# Revit family: LBL-VL
name_source: partatom
category: Lighting Fixtures
units: mm (PartAtom-declared; Revit-internal decimal feet)

## family parameters
Always vertical = Yes
Cut with Voids When Loaded = No
Host = Ceiling
Light Source = Yes
OmniClass Number = 23.80.70.11.14.11
OmniClass Title = Downlights
Part Type = Normal
Room Calculation Point = No
Round Connector Dimension = Use Diameter
Shared = No

## types (8) — shared parameters
Assembly Code = D5020200
Color Filter = 16777215
Description = Commercial-grade, surface or suspended-mounted wrap-around ceiling luminaire
Dimming Lamp Color Temperature Shift = <None>
Housing Finish = Metal - Viscor - White
Lamp = LED
Lens Finish = Polycarbonate - Viscor - Frosted Round
Manufacturer = VISIONEERING by VISCOR
Model = LBL-VL
URL = https://www.viscor.com
Voltage = 120 V
Width = 0' - 8"

## per-type parameters (varying)
| type | Apparent Load | Emit from Line Length | Lamp Wattage | Length | Photometric Web File | Tilt Angle |
| LBL-VL24-LED840K028LUNV | 22 VA | 1' - 11 3/8" | 22 VA | 1' - 11 3/8" | LBL-VL24-LED840K028LUNV.IES | 90.00° |
| LBL-VL24-LED840K037LUNV | 29 VA | 1' - 11 3/8" | 29 VA | 1' - 11 3/8" | LBL-VL24-LED840K037LUNV.IES | 90.00° |
| LBL-VL48-LED840K028LUNV | 22 VA | 3' - 10 1/16" | 22 VA | 3' - 10 1/16" | LBL-VL48-LED840K028LUNV.IES | 90.00° |
| LBL-VL48-LED840K037LUNV | 29 VA | 3' - 10 1/16" | 29 VA | 3' - 10 1/16" | LBL-VL48-LED840K037LUNV.IES | 90.00° |
| LBL-VL48-LED840K045LUNV | 34 VA | 3' - 10 1/16" | 34 VA | 3' - 10 1/16" | LBL-VL48-LED840K045LUNV.IES | 90.00° |
| LBL-VL48-LED840K052LUNV | 40 VA | 3' - 10 1/16" | 40 VA | 3' - 10 1/16" | LBL-VL48-LED840K052LUNV.IES | 60.00° |
| LBL-VL48-LED840K120LUNV | 109 VA | 3' - 10 1/16" | 109 VA | 3' - 10 1/16" | LBL-VL48-LED840K120LUNV.IES | 90.00° |
| LBL-VL96-LED840K240LUNV | 218 VA | 7' - 8 1/8" | 218 VA | 7' - 8 1/8" | LBL-VL96-LED840K240LUNV.ies | 90.00° |

## geometry (parser evidence)
native form markers: Sweep x2
no freeform markers — native parametric forms only
